# Revit family: FAUCET (47)
name_source: partatom
category: Plumbing Fixtures
units: mm (PartAtom-declared; Revit-internal decimal feet)

## family parameters
Always vertical = Yes
Cut with Voids When Loaded = No
OmniClass Number = 23.45.55.14
OmniClass Title = Single Faucets
Part Type = Normal
Room Calculation Point = No
Round Connector Dimension = Use Radius
Shared = No
Work Plane-Based = No

## types (1)
- Polished Chrome
    ADA Compliant = Yes
    Assembly Code = D2010900
    CADworks URL = http://www.CADworks.net
    CW Connection = Yes
    CWFU = 0
    Cold Water Connection NPT = 1"
    Cold Water Connection Radius = 0"
    Default Elevation = 0' - 0"
    Description = Deck-Mounted Bath Faucet
    Finish = Metal - TOTO - Chrome - Polished
    HW Connection = Yes
    HWFU = 0
    Hot Water Connection NPT = 1"
    Hot Water Connection Radius = 0"
    Manufacturer = TOTO
    Model = TB960DD#CP
    Nominal Height = 0' - 3 13/16"
    Nominal Length = 0' - 10 1/8"
    Product URL = http://www.totousa.com
    Series = Soiree
    Shipping Weight = 12.00 lb
    URL = http://www.totousa.com
    Vent Connection = No
    WFU = 0
    Waste Connection = No

## geometry (parser evidence)
native form markers: Sweep x3
no freeform markers — native parametric forms only
